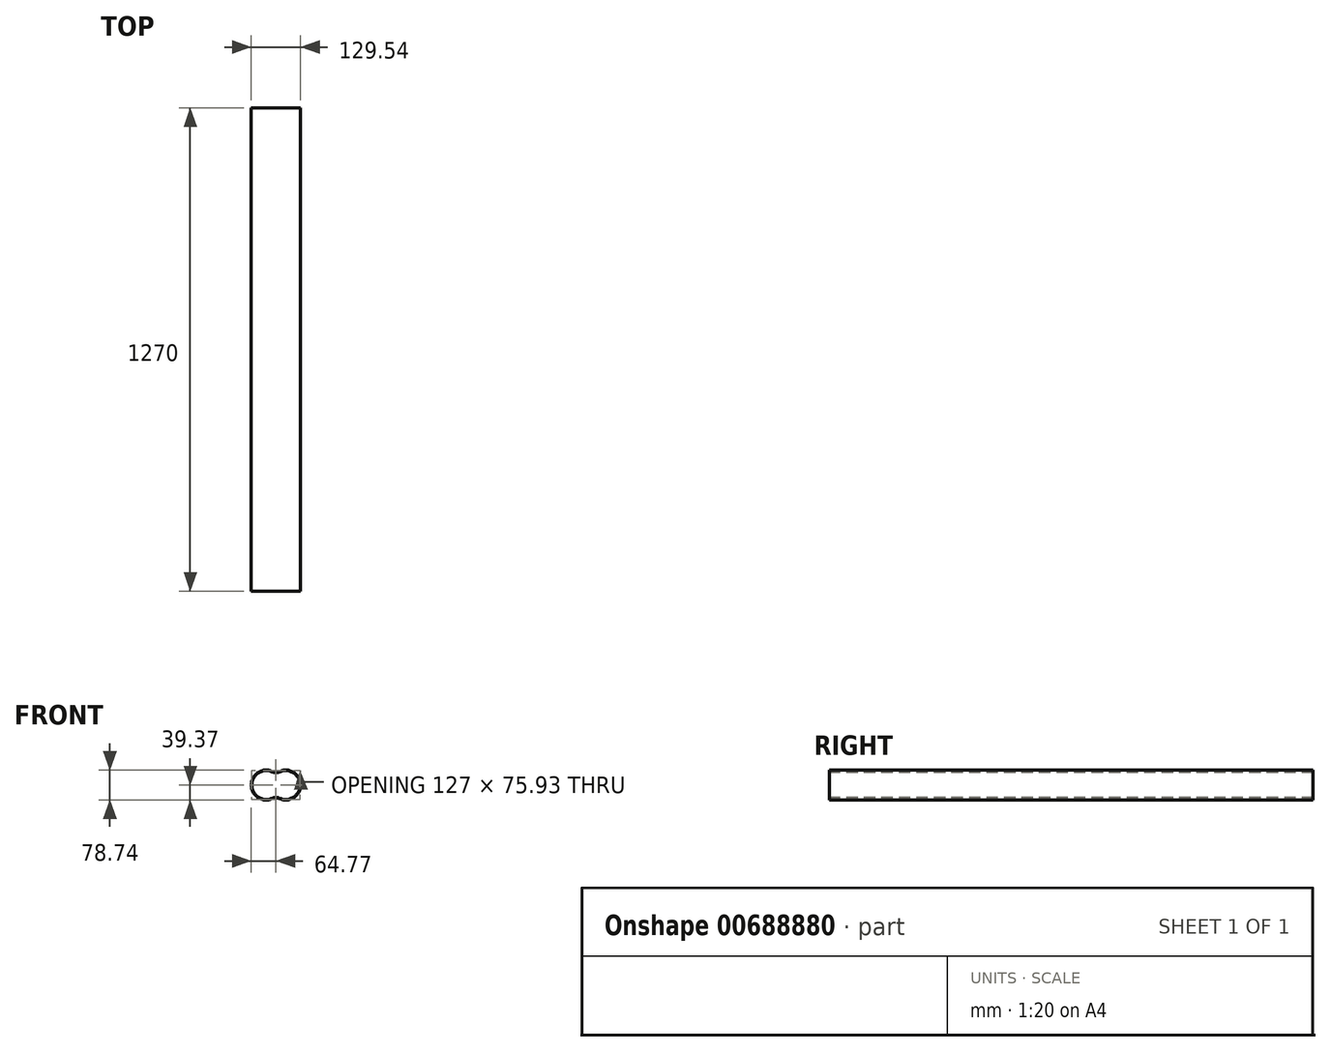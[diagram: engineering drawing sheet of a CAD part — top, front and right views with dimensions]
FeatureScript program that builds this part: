
annotation { "Feature Type Name" : "Feature", "Feature Type Description" : "" }
export const myFeature = defineFeature(function(context is Context, id is Id, definition is map)
    precondition{}
    {
        {
            var Q0;
            Q0=qCreatedBy(makeId("Front.planeOp"),FACE);
            var sketch = newSketch(context, id + "F0", { "sketchPlane" : qUnion([Q0])});
            skCircle(sketch, "E0", {"center": v(0, 0) * mm, "radius": 63.5 * mm, "construction": true});
            skLineSegment(sketch, "E1", {"start": v(0, 0) * mm, "end": v(25.4, 0) * mm, "construction": true});
            skLineSegment(sketch, "E2", {"start": v(0, 0) * mm, "end": v(-25.4, 0) * mm, "construction": true});
            skArc(sketch, "E3", {"start": v(10.16, -34.92) * mm, "mid": v(63.5, 0) * mm, "end": v(10.16, 34.92) * mm});
            skArc(sketch, "E4", {"start": v(-10.16, 34.92) * mm, "mid": v(-63.5, 0) * mm, "end": v(-10.16, -34.92) * mm});
            skPoint(sketch, "E5.visualSharp", {"position": v(0, 28.4) * mm});
            skArc(sketch, "E5.filletArc", {"start": v(-10.16, 34.92) * mm, "mid": v(0, 32.8) * mm, "end": v(10.16, 34.92) * mm});
            skPoint(sketch, "E6.visualSharp", {"position": v(0, -28.4) * mm});
            skArc(sketch, "E6.filletArc", {"start": v(10.16, -34.92) * mm, "mid": v(0, -32.8) * mm, "end": v(-10.16, -34.92) * mm});
            skArc(sketch, "E7.0", {"start": v(-9.65, 36.08) * mm, "mid": v(-64.77, 0) * mm, "end": v(-9.65, -36.08) * mm});
            skArc(sketch, "E7.1", {"start": v(-9.65, 36.08) * mm, "mid": v(0, 34.07) * mm, "end": v(9.65, 36.08) * mm});
            skArc(sketch, "E7.2", {"start": v(9.65, -36.08) * mm, "mid": v(64.77, 0) * mm, "end": v(9.65, 36.08) * mm});
            skArc(sketch, "E7.3", {"start": v(9.65, -36.08) * mm, "mid": v(0, -34.07) * mm, "end": v(-9.65, -36.08) * mm});
            skSolve(sketch);
        }
        {
            var Q0;
            Q0 = qSketchRegion(id + "F0", true);
            extrude(context, id + "F1", {"entities" : qUnion([Q0]), "oppositeDirection" : true, "depth" : 1270 * mm, "offsetDistance" : 25.4 * mm});
        }
    });
